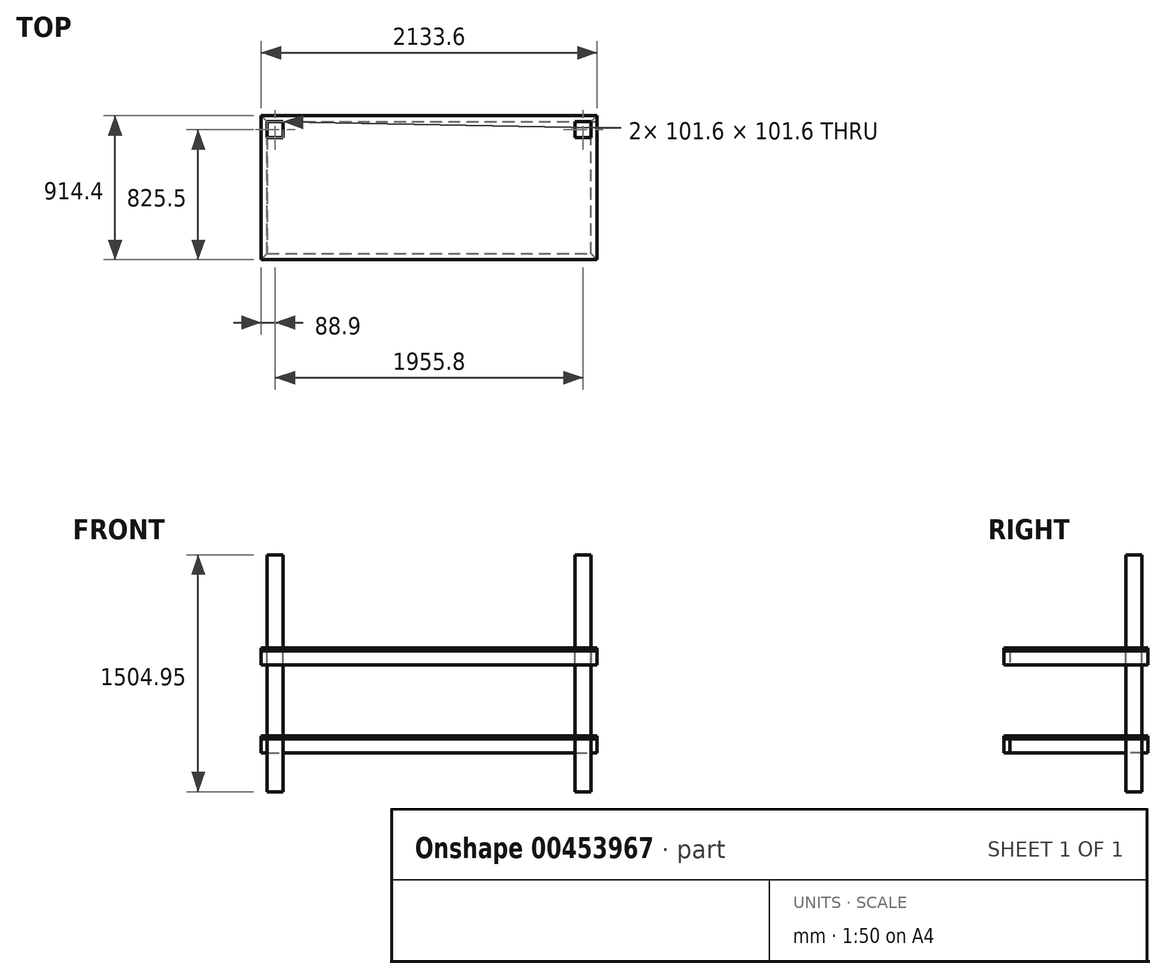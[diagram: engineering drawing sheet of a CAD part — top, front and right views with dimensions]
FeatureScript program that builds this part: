
annotation { "Feature Type Name" : "Feature", "Feature Type Description" : "" }
export const myFeature = defineFeature(function(context is Context, id is Id, definition is map)
    precondition{}
    {
        {
            var Q0;
            Q0=qCreatedBy(makeId("Top.planeOp"),FACE);
            var sketch = newSketch(context, id + "F0", { "sketchPlane" : qUnion([Q0])});
            skLineSegment(sketch, "E0.bottom", {"start": v(-1066.8, -457.2) * mm, "end": v(1066.8, -457.2) * mm});
            skLineSegment(sketch, "E0.top", {"start": v(-1066.8, 457.2) * mm, "end": v(1066.8, 457.2) * mm});
            skLineSegment(sketch, "E0.left", {"start": v(-1066.8, -457.2) * mm, "end": v(-1066.8, 457.2) * mm});
            skLineSegment(sketch, "E0.right", {"start": v(1066.8, -457.2) * mm, "end": v(1066.8, 457.2) * mm});
            skPoint(sketch, "E0.middle", {"position": v(0, 0) * mm});
            skLineSegment(sketch, "E1.bottom", {"start": v(1028.7, 419.1) * mm, "end": v(927.1, 419.1) * mm});
            skLineSegment(sketch, "E1.top", {"start": v(1028.7, 317.5) * mm, "end": v(927.1, 317.5) * mm});
            skLineSegment(sketch, "E1.left", {"start": v(1028.7, 419.1) * mm, "end": v(1028.7, 317.5) * mm});
            skLineSegment(sketch, "E1.right", {"start": v(927.1, 419.1) * mm, "end": v(927.1, 317.5) * mm});
            skPoint(sketch, "E1.middle", {"position": v(977.9, 368.3) * mm});
            skPoint(sketch, "E2.middle", {"position": v(977.9, -368.3) * mm});
            skPoint(sketch, "E3.middle", {"position": v(-977.9, -368.3) * mm});
            skLineSegment(sketch, "E4.bottom", {"start": v(-1028.7, 419.1) * mm, "end": v(-927.1, 419.1) * mm});
            skLineSegment(sketch, "E4.top", {"start": v(-1028.7, 317.5) * mm, "end": v(-927.1, 317.5) * mm});
            skLineSegment(sketch, "E4.left", {"start": v(-1028.7, 419.1) * mm, "end": v(-1028.7, 317.5) * mm});
            skLineSegment(sketch, "E4.right", {"start": v(-927.1, 419.1) * mm, "end": v(-927.1, 317.5) * mm});
            skPoint(sketch, "E4.middle", {"position": v(-977.9, 368.3) * mm});
            skSolve(sketch);
        }
        {
            var Q0;
            Q0=makeQuery(id+"F0.imprint","IMPRINT",FACE,{"disambiguationData":[TD([[makeQuery(id+"F0.imprint","IMPRINT",EDGE,{"derivedFrom":sQuery(id+"F0.wireOp",EDGE,"E0.bottom")}),1.0]])]});
            extrude(context, id + "F1", {"entities" : qUnion([Q0]), "oppositeDirection" : true, "depth" : 19.05 * mm});
        }
        {
            var Q0;
            Q0=makeQuery(id+"F1.opExtrude","SWEPT_FACE",FACE,{"disambiguationData":[OSD([sQuery(id+"F0.wireOp",EDGE,"E0.bottom")])]});
            var sketch = newSketch(context, id + "F2", { "sketchPlane" : qUnion([Q0])});
            skLineSegment(sketch, "E5", {"start": v(-1066.8, -19.05) * mm, "end": v(-1066.8, -107.95) * mm});
            skLineSegment(sketch, "E6", {"start": v(-1066.8, -107.95) * mm, "end": v(1066.8, -107.95) * mm});
            skLineSegment(sketch, "E7", {"start": v(1066.8, -107.95) * mm, "end": v(1066.8, -19.05) * mm});
            skSolve(sketch);
        }
        {
            var Q0;
            Q0=makeQuery(id+"F2.imprint","IMPRINT",FACE,{"disambiguationData":[TD([[makeQuery(id+"F2.imprint","IMPRINT",EDGE,{"derivedFrom":sQuery(id+"F2.wireOp",EDGE,"E5")}),1.0]])]});
            extrude(context, id + "F3", {"entities" : qUnion([Q0]), "oppositeDirection" : true, "depth" : 38.1 * mm});
        }
        {
            var Q0;
            Q0=makeQuery(id+"F3.opExtrude","CAP_EDGE",EDGE,{"disambiguationData":[OSD([sQuery(id+"F2.wireOp",EDGE,"E5")])],"isStart":false});
            chamfer(context, id + "F4", {"entities" : qUnion([Q0]), "width" : 38.1 * mm, "tangentPropagation" : true});
        }
        {
            var Q0;
            Q0=makeQuery(id+"F3.opExtrude","CAP_EDGE",EDGE,{"disambiguationData":[OSD([sQuery(id+"F2.wireOp",EDGE,"E7")])],"isStart":false});
            chamfer(context, id + "F5", {"entities" : qUnion([Q0]), "width" : 38.1 * mm, "tangentPropagation" : true});
        }
        {
            var Q0;
            Q0=makeQuery(id+"F1.opExtrude","SWEPT_FACE",FACE,{"disambiguationData":[OSD([sQuery(id+"F0.wireOp",EDGE,"E0.right")])]});
            var sketch = newSketch(context, id + "F6", { "sketchPlane" : qUnion([Q0])});
            skLineSegment(sketch, "E8", {"start": v(-457.2, -19.05) * mm, "end": v(-457.2, -107.95) * mm});
            skLineSegment(sketch, "E9", {"start": v(-457.2, -107.95) * mm, "end": v(457.2, -107.95) * mm});
            skLineSegment(sketch, "E10", {"start": v(457.2, -107.95) * mm, "end": v(457.2, -19.05) * mm});
            skSolve(sketch);
        }
        {
            var Q0;
            Q0=makeQuery(id+"F6.imprint","IMPRINT",FACE,{"disambiguationData":[TD([[makeQuery(id+"F6.imprint","IMPRINT",EDGE,{"derivedFrom":sQuery(id+"F6.wireOp",EDGE,"E8")}),1.0]])]});
            extrude(context, id + "F7", {"entities" : qUnion([Q0]), "oppositeDirection" : true, "depth" : 38.1 * mm});
        }
        {
            var Q0;
            Q0=makeQuery(id+"F7.opExtrude","CAP_EDGE",EDGE,{"disambiguationData":[OSD([sQuery(id+"F6.wireOp",EDGE,"E8")])],"isStart":false});
            chamfer(context, id + "F8", {"entities" : qUnion([Q0]), "width" : 38.1 * mm, "tangentPropagation" : true});
        }
        {
            var Q0;
            Q0=makeQuery(id+"F7.opExtrude","CAP_EDGE",EDGE,{"disambiguationData":[OSD([sQuery(id+"F6.wireOp",EDGE,"E10")])],"isStart":false});
            chamfer(context, id + "F9", {"entities" : qUnion([Q0]), "width" : 38.1 * mm, "tangentPropagation" : true});
        }
        {
            var Q0;
            Q0=makeQuery(id+"F1.opExtrude","SWEPT_FACE",FACE,{"disambiguationData":[OSD([sQuery(id+"F0.wireOp",EDGE,"E0.top")])]});
            var sketch = newSketch(context, id + "F10", { "sketchPlane" : qUnion([Q0])});
            skLineSegment(sketch, "E11", {"start": v(-1066.8, -19.05) * mm, "end": v(-1066.8, -107.95) * mm});
            skLineSegment(sketch, "E12", {"start": v(-1066.8, -107.95) * mm, "end": v(1066.8, -107.95) * mm});
            skLineSegment(sketch, "E13", {"start": v(1066.8, -107.95) * mm, "end": v(1066.8, -19.05) * mm});
            skSolve(sketch);
        }
        {
            var Q0;
            Q0=makeQuery(id+"F10.imprint","IMPRINT",FACE,{"disambiguationData":[TD([[makeQuery(id+"F10.imprint","IMPRINT",EDGE,{"derivedFrom":sQuery(id+"F10.wireOp",EDGE,"E11")}),1.0]])]});
            extrude(context, id + "F11", {"entities" : qUnion([Q0]), "oppositeDirection" : true, "depth" : 38.1 * mm});
        }
        {
            var Q0;
            Q0=makeQuery(id+"F11.opExtrude","CAP_EDGE",EDGE,{"disambiguationData":[OSD([sQuery(id+"F10.wireOp",EDGE,"E11")])],"isStart":false});
            chamfer(context, id + "F12", {"entities" : qUnion([Q0]), "width" : 38.1 * mm, "tangentPropagation" : true});
        }
        {
            var Q0;
            Q0=makeQuery(id+"F11.opExtrude","CAP_EDGE",EDGE,{"disambiguationData":[OSD([sQuery(id+"F10.wireOp",EDGE,"E13")])],"isStart":false});
            chamfer(context, id + "F13", {"entities" : qUnion([Q0]), "width" : 38.1 * mm, "tangentPropagation" : true});
        }
        {
            var Q0;
            Q0=makeQuery(id+"F1.opExtrude","SWEPT_FACE",FACE,{"disambiguationData":[OSD([sQuery(id+"F0.wireOp",EDGE,"E0.left")])]});
            var sketch = newSketch(context, id + "F14", { "sketchPlane" : qUnion([Q0])});
            skLineSegment(sketch, "E14", {"start": v(-457.2, -19.05) * mm, "end": v(-457.2, -107.95) * mm});
            skLineSegment(sketch, "E15", {"start": v(-457.2, -107.95) * mm, "end": v(457.2, -107.95) * mm});
            skLineSegment(sketch, "E16", {"start": v(457.2, -107.95) * mm, "end": v(457.2, -19.05) * mm});
            skSolve(sketch);
        }
        {
            var Q0;
            Q0=makeQuery(id+"F14.imprint","IMPRINT",FACE,{"disambiguationData":[TD([[makeQuery(id+"F14.imprint","IMPRINT",EDGE,{"derivedFrom":sQuery(id+"F14.wireOp",EDGE,"E14")}),1.0]])]});
            extrude(context, id + "F15", {"entities" : qUnion([Q0]), "oppositeDirection" : true, "depth" : 38.1 * mm});
        }
        {
            var Q0;
            Q0=makeQuery(id+"F15.opExtrude","CAP_EDGE",EDGE,{"disambiguationData":[OSD([sQuery(id+"F14.wireOp",EDGE,"E14")])],"isStart":false});
            var Q1;
            Q1=makeQuery(id+"F15.opExtrude","CAP_EDGE",EDGE,{"disambiguationData":[OSD([sQuery(id+"F14.wireOp",EDGE,"E16")])],"isStart":false});
            chamfer(context, id + "F16", {"entities" : qUnion([Q0, Q1]), "width" : 38.1 * mm, "tangentPropagation" : true});
        }
        {
            var Q0;
            Q0=makeQuery(id+"F0.imprint","IMPRINT",FACE,{"disambiguationData":[TD([[makeQuery(id+"F0.imprint","IMPRINT",EDGE,{"derivedFrom":sQuery(id+"F0.wireOp",EDGE,"E4.bottom")}),-1.0]])]});
            var Q1;
            Q1=makeQuery(id+"F0.imprint","IMPRINT",FACE,{"disambiguationData":[TD([[makeQuery(id+"F0.imprint","IMPRINT",EDGE,{"derivedFrom":sQuery(id+"F0.wireOp",EDGE,"E1.bottom")}),1.0]])]});
            extrude(context, id + "F17", {"entities" : qUnion([Q0, Q1]), "oppositeDirection" : true, "depth" : 914.4 * mm, "hasSecondDirection" : true, "secondDirectionOppositeDirection" : false, "secondDirectionDepth" : 590.55 * mm});
        }
        {
            var Q0;
            Q0=makeQuery(id+"F15.opExtrude","CAP_FACE",FACE,{"disambiguationData":[OSD([sQuery(id+"F0.wireOp",EDGE,"E0.left"),sQuery(id+"F14.wireOp",EDGE,"E14"),sQuery(id+"F14.wireOp",EDGE,"E15"),sQuery(id+"F14.wireOp",EDGE,"E16")])],"isStart":true});
            var sketch = newSketch(context, id + "F18", { "sketchPlane" : qUnion([Q0])});
            skLineSegment(sketch, "E17", {"start": v(457.2, -107.95) * mm, "end": v(457.2, -558.8) * mm});
            skLineSegment(sketch, "E18", {"start": v(457.2, -558.8) * mm, "end": v(-457.2, -558.8) * mm});
            skLineSegment(sketch, "E19", {"start": v(-457.2, -558.8) * mm, "end": v(-457.2, -107.95) * mm});
            skLineSegment(sketch, "E20.bottom", {"start": v(-457.2, -558.8) * mm, "end": v(457.2, -558.8) * mm});
            skLineSegment(sketch, "E20.top", {"start": v(-457.2, -577.85) * mm, "end": v(457.2, -577.85) * mm});
            skLineSegment(sketch, "E20.left", {"start": v(-457.2, -558.8) * mm, "end": v(-457.2, -577.85) * mm});
            skLineSegment(sketch, "E20.right", {"start": v(457.2, -558.8) * mm, "end": v(457.2, -577.85) * mm});
            skLineSegment(sketch, "E21.top", {"start": v(-457.2, -666.75) * mm, "end": v(457.2, -666.75) * mm});
            skLineSegment(sketch, "E21.left", {"start": v(-457.2, -577.85) * mm, "end": v(-457.2, -666.75) * mm});
            skLineSegment(sketch, "E21.right", {"start": v(457.2, -577.85) * mm, "end": v(457.2, -666.75) * mm});
            skSolve(sketch);
        }
        {
            var Q0;
            Q0=makeQuery(id+"F18.imprint","IMPRINT",FACE,{"disambiguationData":[TD([[makeQuery(id+"F18.imprint","IMPRINT",EDGE,{"derivedFrom":sQuery(id+"F18.wireOp",EDGE,"E20.top")}),-1.0]])]});
            extrude(context, id + "F19", {"entities" : qUnion([Q0]), "operationType" : NewBodyOperationType.ADD, "oppositeDirection" : true, "depth" : 38.1 * mm});
        }
        {
            var Q0;
            Q0=makeQuery(id+"F19.opExtrude","CAP_EDGE",EDGE,{"disambiguationData":[OSD([sQuery(id+"F18.wireOp",EDGE,"E21.right")])],"isStart":false});
            var Q1;
            Q1=makeQuery(id+"F19.opExtrude","CAP_EDGE",EDGE,{"disambiguationData":[OSD([sQuery(id+"F18.wireOp",EDGE,"E21.left")])],"isStart":false});
            chamfer(context, id + "F20", {"entities" : qUnion([Q0, Q1]), "width" : 38.1 * mm, "tangentPropagation" : true});
        }
        {
            var Q0;
            Q0=makeQuery(id+"F11.opExtrude","CAP_FACE",FACE,{"disambiguationData":[OSD([sQuery(id+"F0.wireOp",EDGE,"E0.top"),sQuery(id+"F10.wireOp",EDGE,"E11"),sQuery(id+"F10.wireOp",EDGE,"E12"),sQuery(id+"F10.wireOp",EDGE,"E13")])],"isStart":true});
            var sketch = newSketch(context, id + "F21", { "sketchPlane" : qUnion([Q0])});
            skLineSegment(sketch, "E22.bottom", {"start": v(1066.8, -107.95) * mm, "end": v(-1066.8, -107.95) * mm});
            skLineSegment(sketch, "E22.top", {"start": v(1066.8, -558.8) * mm, "end": v(-1066.8, -558.8) * mm});
            skLineSegment(sketch, "E22.left", {"start": v(1066.8, -107.95) * mm, "end": v(1066.8, -558.8) * mm});
            skLineSegment(sketch, "E22.right", {"start": v(-1066.8, -107.95) * mm, "end": v(-1066.8, -558.8) * mm});
            skLineSegment(sketch, "E23.top", {"start": v(1066.8, -577.85) * mm, "end": v(-1066.8, -577.85) * mm});
            skLineSegment(sketch, "E23.left", {"start": v(1066.8, -558.8) * mm, "end": v(1066.8, -577.85) * mm});
            skLineSegment(sketch, "E23.right", {"start": v(-1066.8, -558.8) * mm, "end": v(-1066.8, -577.85) * mm});
            skLineSegment(sketch, "E24.top", {"start": v(1066.8, -666.75) * mm, "end": v(-1066.8, -666.75) * mm});
            skLineSegment(sketch, "E24.left", {"start": v(1066.8, -577.85) * mm, "end": v(1066.8, -666.75) * mm});
            skLineSegment(sketch, "E24.right", {"start": v(-1066.8, -577.85) * mm, "end": v(-1066.8, -666.75) * mm});
            skSolve(sketch);
        }
        {
            var Q0;
            Q0=makeQuery(id+"F19.opExtrude","SWEPT_FACE",FACE,{"disambiguationData":[OSD([sQuery(id+"F18.wireOp",EDGE,"E20.top")])]});
            var sketch = newSketch(context, id + "F22", { "sketchPlane" : qUnion([Q0])});
            skLineSegment(sketch, "E25.bottom", {"start": v(-1066.8, 457.2) * mm, "end": v(1066.8, 457.2) * mm});
            skLineSegment(sketch, "E25.top", {"start": v(-1066.8, -457.2) * mm, "end": v(1066.8, -457.2) * mm});
            skLineSegment(sketch, "E25.left", {"start": v(-1066.8, 457.2) * mm, "end": v(-1066.8, -457.2) * mm});
            skLineSegment(sketch, "E25.right", {"start": v(1066.8, 457.2) * mm, "end": v(1066.8, -457.2) * mm});
            skLineSegment(sketch, "E26.bottom", {"start": v(-1028.7, 317.5) * mm, "end": v(-927.1, 317.5) * mm});
            skLineSegment(sketch, "E26.top", {"start": v(-1028.7, 419.1) * mm, "end": v(-927.1, 419.1) * mm});
            skLineSegment(sketch, "E26.left", {"start": v(-1028.7, 317.5) * mm, "end": v(-1028.7, 419.1) * mm});
            skLineSegment(sketch, "E26.right", {"start": v(-927.1, 317.5) * mm, "end": v(-927.1, 419.1) * mm});
            skLineSegment(sketch, "E27", {"start": v(-1028.7, -419.1) * mm, "end": v(-1066.8, -457.2) * mm});
            skLineSegment(sketch, "E28", {"start": v(-1028.7, -419.1) * mm, "end": v(-1028.7, 419.1) * mm});
            skLineSegment(sketch, "E29", {"start": v(-1028.7, 419.1) * mm, "end": v(-1066.8, 457.2) * mm});
            skSolve(sketch);
        }
        {
            var Q0;
            Q0=makeQuery(id+"F22.imprint","IMPRINT",FACE,{"disambiguationData":[TD([[makeQuery(id+"F22.imprint","IMPRINT",EDGE,{"derivedFrom":sQuery(id+"F22.wireOp",EDGE,"E25.bottom")}),-1.0]])]});
            extrude(context, id + "F23", {"entities" : qUnion([Q0]), "depth" : 19.05 * mm});
        }
        {
            var Q0;
            Q0=makeQuery(id+"F21.imprint","IMPRINT",FACE,{"disambiguationData":[TD([[makeQuery(id+"F21.imprint","IMPRINT",EDGE,{"derivedFrom":sQuery(id+"F21.wireOp",EDGE,"E23.top")}),1.0]])]});
            extrude(context, id + "F24", {"entities" : qUnion([Q0]), "oppositeDirection" : true, "depth" : 38.1 * mm});
        }
        {
            var Q0;
            Q0=makeQuery(id+"F24.opExtrude","CAP_EDGE",EDGE,{"disambiguationData":[OSD([sQuery(id+"F21.wireOp",EDGE,"E24.left")])],"isStart":false});
            chamfer(context, id + "F25", {"entities" : qUnion([Q0]), "width" : 38.1 * mm, "tangentPropagation" : true});
        }
    });
